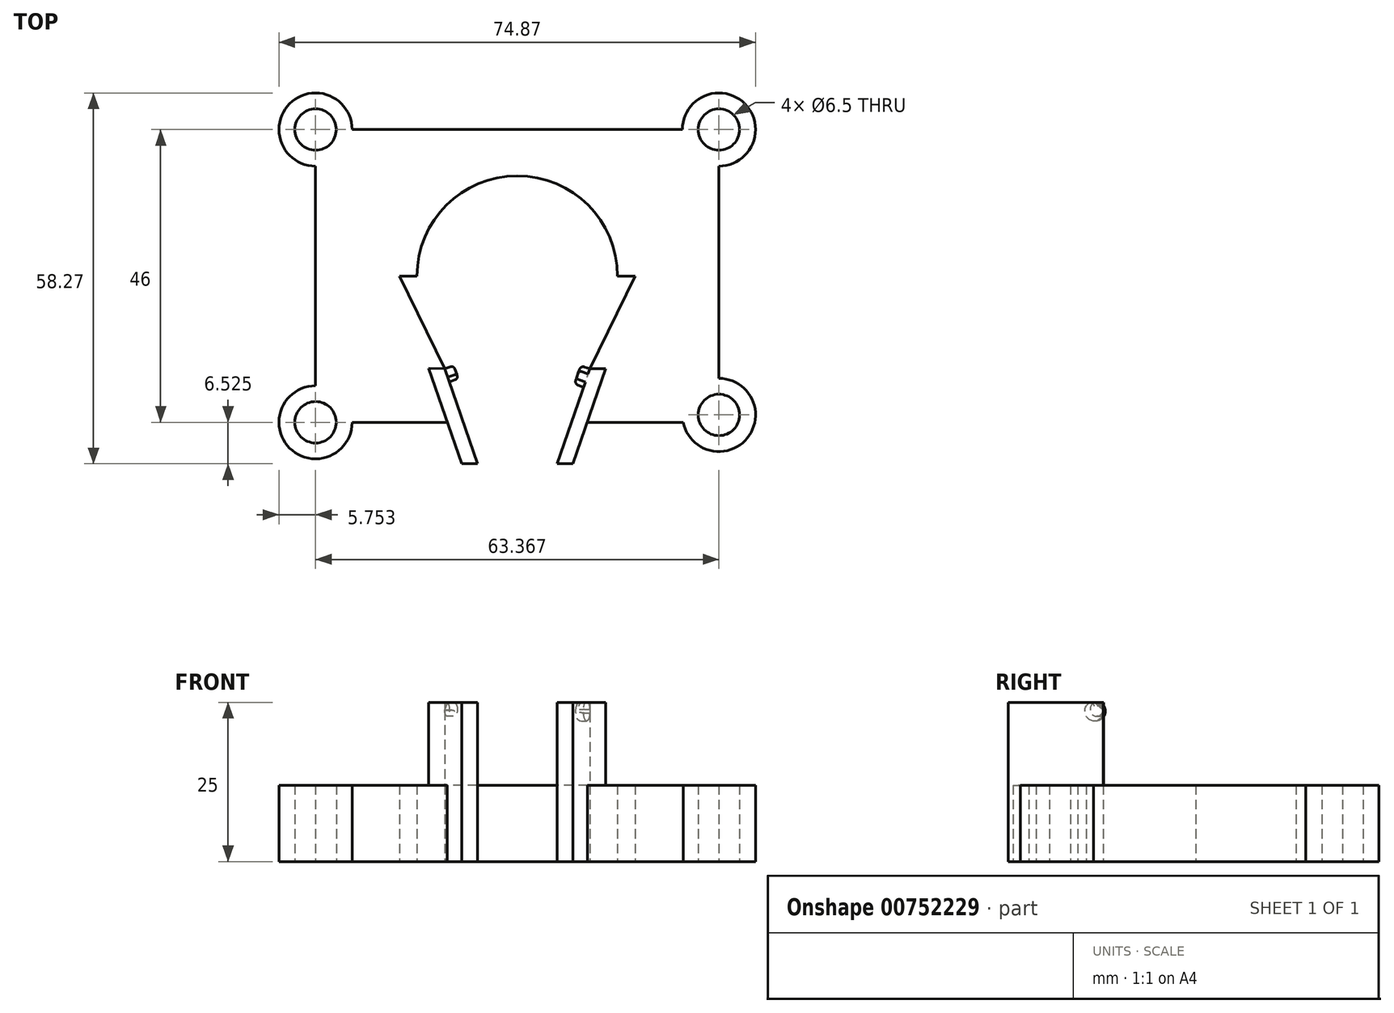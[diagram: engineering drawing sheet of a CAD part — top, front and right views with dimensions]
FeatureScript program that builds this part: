
annotation { "Feature Type Name" : "Feature", "Feature Type Description" : "" }
export const myFeature = defineFeature(function(context is Context, id is Id, definition is map)
    precondition{}
    {
        {
            var Q0;
            Q0=qCreatedBy(makeId("Top.planeOp"),FACE);
            var sketch = newSketch(context, id + "F0", { "sketchPlane" : qUnion([Q0])});
            skLineSegment(sketch, "E0.bottom", {"start": v(-52.57, 38.18) * mm, "end": v(4.3, 38.18) * mm});
            skLineSegment(sketch, "E0.left", {"start": v(-55.82, 34.93) * mm, "end": v(-55.82, -4.57) * mm});
            skLineSegment(sketch, "E0.right", {"start": v(7.55, 34.93) * mm, "end": v(7.55, -3.4) * mm});
            skCircle(sketch, "E1", {"center": v(7.55, 38.18) * mm, "radius": 3.25 * mm});
            skCircle(sketch, "E2", {"center": v(-55.82, 38.18) * mm, "radius": 3.25 * mm});
            skCircle(sketch, "E3", {"center": v(-55.82, -7.82) * mm, "radius": 3.25 * mm});
            skCircle(sketch, "E4", {"center": v(7.55, -6.66) * mm, "radius": 3.25 * mm});
            skCircle(sketch, "E5", {"center": v(-55.82, 38.18) * mm, "radius": 5.75 * mm});
            skCircle(sketch, "E6", {"center": v(7.55, 38.18) * mm, "radius": 5.75 * mm});
            skCircle(sketch, "E7", {"center": v(7.55, -6.66) * mm, "radius": 5.75 * mm});
            skCircle(sketch, "E8", {"center": v(-55.82, -7.82) * mm, "radius": 5.75 * mm});
            skPoint(sketch, "E9.first.point", {"position": v(-24.13, 38.18) * mm});
            skPoint(sketch, "E9.second.point", {"position": v(-55.82, 15.18) * mm});
            skPoint(sketch, "E10.middle", {"position": v(-24.13, 15.17) * mm});
            skCircle(sketch, "E11", {"center": v(-24.13, 15.17) * mm, "radius": 15.75 * mm});
            skArc(sketch, "E12", {"start": v(-5.63, 15.17) * mm, "mid": v(-24.13, 33.67) * mm, "end": v(-42.63, 15.17) * mm});
            skLineSegment(sketch, "E13", {"start": v(-24.13, -7.82) * mm, "end": v(-24.13, -7.85) * mm});
            skLineSegment(sketch, "E14", {"start": v(-35.53, 0.6) * mm, "end": v(-30.38, -14.34) * mm});
            skLineSegment(sketch, "E15", {"start": v(-17.88, -14.34) * mm, "end": v(-12.74, 0.6) * mm});
            skLineSegment(sketch, "E16", {"start": v(-30.38, -14.34) * mm, "end": v(-32.88, -14.34) * mm});
            skLineSegment(sketch, "E17", {"start": v(-32.88, -14.34) * mm, "end": v(-38.03, 0.64) * mm});
            skLineSegment(sketch, "E18", {"start": v(-38.03, 0.64) * mm, "end": v(-35.53, 0.6) * mm});
            skLineSegment(sketch, "E19", {"start": v(-17.88, -14.34) * mm, "end": v(-15.38, -14.34) * mm});
            skLineSegment(sketch, "E20", {"start": v(-15.38, -14.34) * mm, "end": v(-10.24, 0.6) * mm});
            skLineSegment(sketch, "E21", {"start": v(-10.24, 0.6) * mm, "end": v(-12.74, 0.6) * mm});
            skLineSegment(sketch, "E22.trimOffspring", {"start": v(-55.82, -7.82) * mm, "end": v(-55.82, -7.85) * mm});
            skLineSegment(sketch, "E23.trimOffspring", {"start": v(7.55, 38.18) * mm, "end": v(7.55, 38.18) * mm});
            skPoint(sketch, "E24.orphan", {"position": v(-24.13, -14.34) * mm});
            skLineSegment(sketch, "E25", {"start": v(-24.13, 15.17) * mm, "end": v(-42.63, 15.17) * mm});
            skLineSegment(sketch, "E26", {"start": v(-35.53, 0.6) * mm, "end": v(-42.63, 15.17) * mm});
            skLineSegment(sketch, "E27", {"start": v(-24.13, 15.17) * mm, "end": v(-5.63, 15.17) * mm});
            skLineSegment(sketch, "E28", {"start": v(-12.74, 0.6) * mm, "end": v(-5.63, 15.17) * mm});
            skLineSegment(sketch, "E29", {"start": v(-30.38, -14.34) * mm, "end": v(-17.88, -14.34) * mm});
            skLineSegment(sketch, "E30", {"start": v(-42.63, 15.17) * mm, "end": v(-55.82, 15.18) * mm});
            skLineSegment(sketch, "E31", {"start": v(-5.63, 15.17) * mm, "end": v(7.55, 15.17) * mm});
            skLineSegment(sketch, "E32", {"start": v(-24.13, 15.17) * mm, "end": v(-24.13, -14.34) * mm});
            skLineSegment(sketch, "E33", {"start": v(-24.13, 15.17) * mm, "end": v(-24.13, 38.18) * mm});
            skLineSegment(sketch, "E34", {"start": v(-35.53, 0.6) * mm, "end": v(-12.74, 0.6) * mm});
            skLineSegment(sketch, "E35", {"start": v(-24.13, -7.82) * mm, "end": v(1.92, -7.82) * mm});
            skLineSegment(sketch, "E36", {"start": v(-24.13, -7.82) * mm, "end": v(-50.07, -7.82) * mm});
            skSolve(sketch);
        }
        {
            var Q0;
            {var subQ0=sQuery(id+"F0.wireOp",EDGE,"E30");Q0=makeQuery(id+"F0.imprint","IMPRINT",FACE,{"disambiguationData":[TD([[makeQuery(id+"F0.imprint","IMPRINT",EDGE,{"derivedFrom":subQ0}),-1.0]])]});}
            var Q1;
            {var subQ0=sQuery(id+"F0.wireOp",EDGE,"E0.bottom");var subQ1=sQuery(id+"F0.wireOp",EDGE,"E2");var subQ2=makeQuery(id+"F0.imprint","INTERSECT",VERTEX,{"derivedFrom":[subQ1,subQ0]});Q1=makeQuery(id+"F0.imprint","IMPRINT",FACE,{"disambiguationData":[TD([[makeQuery(id+"F0.imprint","IMPRINT",EDGE,{"disambiguationData":[TD([[subQ2,1.0]])],"derivedFrom":subQ1}),-1.0]])]});}
            var Q2;
            {var subQ0=sQuery(id+"F0.wireOp",EDGE,"E0.bottom");var subQ1=sQuery(id+"F0.wireOp",EDGE,"E2");var subQ2=makeQuery(id+"F0.imprint","INTERSECT",VERTEX,{"derivedFrom":[subQ1,subQ0]});Q2=makeQuery(id+"F0.imprint","IMPRINT",FACE,{"disambiguationData":[TD([[makeQuery(id+"F0.imprint","IMPRINT",EDGE,{"disambiguationData":[TD([[subQ2,-1.0]])],"derivedFrom":subQ1}),-1.0]])]});}
            var Q3;
            {var subQ0=sQuery(id+"F0.wireOp",EDGE,"E31");Q3=makeQuery(id+"F0.imprint","IMPRINT",FACE,{"disambiguationData":[TD([[makeQuery(id+"F0.imprint","IMPRINT",EDGE,{"derivedFrom":subQ0}),1.0]])]});}
            var Q4;
            {var subQ0=sQuery(id+"F0.wireOp",EDGE,"E33");var subQ1=sQuery(id+"F0.wireOp",EDGE,"E11");var subQ2=makeQuery(id+"F0.imprint","INTERSECT",VERTEX,{"derivedFrom":[subQ1,subQ0]});Q4=makeQuery(id+"F0.imprint","IMPRINT",FACE,{"disambiguationData":[TD([[makeQuery(id+"F0.imprint","IMPRINT",EDGE,{"disambiguationData":[TD([[subQ2,1.0]])],"derivedFrom":subQ1}),-1.0]])]});}
            var Q5;
            {var subQ0=sQuery(id+"F0.wireOp",EDGE,"E33");var subQ1=sQuery(id+"F0.wireOp",EDGE,"E11");var subQ2=makeQuery(id+"F0.imprint","INTERSECT",VERTEX,{"derivedFrom":[subQ1,subQ0]});Q5=makeQuery(id+"F0.imprint","IMPRINT",FACE,{"disambiguationData":[TD([[makeQuery(id+"F0.imprint","IMPRINT",EDGE,{"disambiguationData":[TD([[subQ2,-1.0]])],"derivedFrom":subQ1}),-1.0]])]});}
            var Q6;
            {var subQ0=sQuery(id+"F0.wireOp",EDGE,"E0.bottom");var subQ1=sQuery(id+"F0.wireOp",EDGE,"E1");var subQ2=makeQuery(id+"F0.imprint","INTERSECT",VERTEX,{"derivedFrom":[subQ1,subQ0]});Q6=makeQuery(id+"F0.imprint","IMPRINT",FACE,{"disambiguationData":[TD([[makeQuery(id+"F0.imprint","IMPRINT",EDGE,{"disambiguationData":[TD([[subQ2,1.0]])],"derivedFrom":subQ1}),-1.0]])]});}
            var Q7;
            {var subQ0=sQuery(id+"F0.wireOp",EDGE,"E0.bottom");var subQ1=sQuery(id+"F0.wireOp",EDGE,"E1");var subQ2=makeQuery(id+"F0.imprint","INTERSECT",VERTEX,{"derivedFrom":[subQ1,subQ0]});Q7=makeQuery(id+"F0.imprint","IMPRINT",FACE,{"disambiguationData":[TD([[makeQuery(id+"F0.imprint","IMPRINT",EDGE,{"disambiguationData":[TD([[subQ2,-1.0]])],"derivedFrom":subQ1}),-1.0]])]});}
            var Q8;
            {var subQ0=sQuery(id+"F0.wireOp",EDGE,"E0.right");var subQ1=sQuery(id+"F0.wireOp",EDGE,"E4");var subQ2=makeQuery(id+"F0.imprint","INTERSECT",VERTEX,{"derivedFrom":[subQ1,subQ0]});Q8=makeQuery(id+"F0.imprint","IMPRINT",FACE,{"disambiguationData":[TD([[makeQuery(id+"F0.imprint","IMPRINT",EDGE,{"disambiguationData":[TD([[subQ2,1.0]])],"derivedFrom":subQ1}),-1.0]])]});}
            var Q9;
            {var subQ0=sQuery(id+"F0.wireOp",EDGE,"E0.right");var subQ1=sQuery(id+"F0.wireOp",EDGE,"E4");var subQ2=makeQuery(id+"F0.imprint","INTERSECT",VERTEX,{"derivedFrom":[subQ1,subQ0]});Q9=makeQuery(id+"F0.imprint","IMPRINT",FACE,{"disambiguationData":[TD([[makeQuery(id+"F0.imprint","IMPRINT",EDGE,{"disambiguationData":[TD([[subQ2,-1.0]])],"derivedFrom":subQ1}),-1.0]])]});}
            var Q10;
            Q10=makeQuery(id+"F0.imprint","IMPRINT",FACE,{"disambiguationData":[TD([[makeQuery(id+"F0.imprint","IMPRINT",EDGE,{"derivedFrom":sQuery(id+"F0.wireOp",EDGE,"E15")}),-1.0]])]});
            var Q11;
            {var subQ0=sQuery(id+"F0.wireOp",EDGE,"E21");Q11=makeQuery(id+"F0.imprint","IMPRINT",FACE,{"disambiguationData":[TD([[makeQuery(id+"F0.imprint","IMPRINT",EDGE,{"derivedFrom":subQ0}),-1.0]])]});}
            var Q12;
            {var subQ8=sQuery(id+"F0.wireOp",EDGE,"E18");Q12=makeQuery(id+"F0.imprint","IMPRINT",FACE,{"disambiguationData":[TD([[makeQuery(id+"F0.imprint","IMPRINT",EDGE,{"derivedFrom":subQ8}),1.0]])]});}
            var Q13;
            {var subQ0=sQuery(id+"F0.wireOp",EDGE,"E3");var subQ1=sQuery(id+"F0.wireOp",EDGE,"E0.top");var subQ2=makeQuery(id+"F0.imprint","INTERSECT",VERTEX,{"derivedFrom":[subQ1,subQ0]});Q13=makeQuery(id+"F0.imprint","IMPRINT",FACE,{"disambiguationData":[TD([[makeQuery(id+"F0.imprint","IMPRINT",EDGE,{"disambiguationData":[TD([[subQ2,-1.0]])],"derivedFrom":subQ1}),1.0]])]});}
            var Q14;
            {var subQ0=sQuery(id+"F0.wireOp",EDGE,"E10.top");var subQ1=sQuery(id+"F0.wireOp",EDGE,"E3");var subQ2=makeQuery(id+"F0.imprint","INTERSECT",VERTEX,{"derivedFrom":[subQ1,subQ0]});Q14=makeQuery(id+"F0.imprint","IMPRINT",FACE,{"disambiguationData":[TD([[makeQuery(id+"F0.imprint","IMPRINT",EDGE,{"disambiguationData":[TD([[subQ2,1.0]])],"derivedFrom":subQ1}),-1.0]])]});}
            var Q15;
            Q15=makeQuery(id+"F0.imprint","IMPRINT",FACE,{"disambiguationData":[TD([[makeQuery(id+"F0.imprint","IMPRINT",EDGE,{"derivedFrom":sQuery(id+"F0.wireOp",EDGE,"E14")}),-1.0]])]});
            extrude(context, id + "F1", {"entities" : qUnion([Q0, Q1, Q2, Q3, Q4, Q5, Q6, Q7, Q8, Q9, Q10, Q11, Q12, Q13, Q14, Q15]), "depth" : 12 * mm, "offsetDistance" : 25 * mm});
        }
        {
            var Q0;
            Q0=makeQuery(id+"F0.imprint","IMPRINT",FACE,{"disambiguationData":[TD([[makeQuery(id+"F0.imprint","IMPRINT",EDGE,{"derivedFrom":sQuery(id+"F0.wireOp",EDGE,"E14")}),-1.0]])]});
            var Q1;
            Q1=makeQuery(id+"F0.imprint","IMPRINT",FACE,{"disambiguationData":[TD([[makeQuery(id+"F0.imprint","IMPRINT",EDGE,{"derivedFrom":sQuery(id+"F0.wireOp",EDGE,"E15")}),-1.0]])]});
            extrude(context, id + "F2", {"entities" : qUnion([Q0, Q1]), "operationType" : NewBodyOperationType.ADD, "depth" : 25 * mm, "offsetDistance" : 25 * mm});
        }
        {
            var Q0;
            {var subQ0=sQuery(id+"F0.wireOp",EDGE,"E14");Q0=makeQuery(id+"F2.boolean.opBoolean","MERGE",FACE,{"derivedFrom":[makeQuery(id+"F1.opExtrude","SWEPT_FACE",FACE,{"disambiguationData":[OSD([subQ0])]}),makeQuery(id+"F2.opExtrude","SWEPT_FACE",FACE,{"disambiguationData":[OSD([subQ0])]})]});}
            var sketch = newSketch(context, id + "F3", { "sketchPlane" : qUnion([Q0])});
            skSolve(sketch);
        }
        {
            var Q0;
            {var subQ2=sQuery(id+"F0.wireOp",EDGE,"E14");Q0=makeQuery(id+"F3.imprint","IMPRINT",FACE,{"disambiguationData":[TD([[makeQuery(id+"F3.imprint","IMPRINT",EDGE,{"derivedFrom":makeQuery(id+"F1.opExtrude","CAP_EDGE",EDGE,{"disambiguationData":[OSD([subQ2])],"isStart":true})}),-1.0]])]});}
            var sketch = newSketch(context, id + "F4", { "sketchPlane" : qUnion([Q0])});
            skArc(sketch, "E37", {"start": v(10.74, 24.97) * mm, "mid": v(10.35, 23.1) * mm, "end": v(12.14, 23.77) * mm});
            skLineSegment(sketch, "E38", {"start": v(12.14, 23.77) * mm, "end": v(10.74, 24.97) * mm});
            skSolve(sketch);
        }
        {
            var Q0;
            {var subQ0=sQuery(id+"F4.wireOp",EDGE,"E38");var subQ1=sQuery(id+"F4.wireOp",EDGE,"E37");var subQ2=makeQuery(id+"F4.imprint","INTERSECT",VERTEX,{"disambiguationData":[OD(0.0)],"derivedFrom":[subQ1,subQ0]});Q0=makeQuery(id+"F4.imprint","IMPRINT",FACE,{"disambiguationData":[TD([[makeQuery(id+"F4.imprint","IMPRINT",EDGE,{"disambiguationData":[TD([[subQ2,-1.0]])],"derivedFrom":subQ1}),1.0]])]});}
            extrude(context, id + "F5", {"entities" : qUnion([Q0]), "operationType" : NewBodyOperationType.ADD, "depth" : 1.5 * mm, "offsetDistance" : 25 * mm});
        }
        {
            var Q0;
            Q0=makeQuery(id+"F5.opExtrude","CAP_EDGE",EDGE,{"disambiguationData":[OSD([sQuery(id+"F4.wireOp",EDGE,"E38")])],"isStart":false});
            var Q1;
            Q1=makeQuery(id+"F5.opExtrude","CAP_EDGE",EDGE,{"disambiguationData":[OSD([sQuery(id+"F4.wireOp",EDGE,"E37")])],"isStart":false});
            fillet(context, id + "F6", {"entities" : qUnion([Q0, Q1]), "radius" : 0.5 * mm, "tangentPropagation" : true, "allowEdgeOverflow" : false});
        }
        {
            var Q0;
            {var subQ0=sQuery(id+"F0.wireOp",EDGE,"E15");Q0=makeQuery(id+"F2.boolean.opBoolean","MERGE",FACE,{"derivedFrom":[makeQuery(id+"F1.opExtrude","SWEPT_FACE",FACE,{"disambiguationData":[OSD([subQ0])]}),makeQuery(id+"F2.opExtrude","SWEPT_FACE",FACE,{"disambiguationData":[OSD([subQ0])]})]});}
            var sketch = newSketch(context, id + "F7", { "sketchPlane" : qUnion([Q0])});
            skCircle(sketch, "E39", {"center": v(5.1, 23.62) * mm, "radius": 1.53 * mm});
            skPoint(sketch, "E39.first.point", {"position": v(5.77, 25) * mm});
            skPoint(sketch, "E39.second.point", {"position": v(3.6, 23.36) * mm});
            skPoint(sketch, "E39.third.point", {"position": v(6.31, 22.69) * mm});
            skSolve(sketch);
        }
        {
            var Q0;
            {var subQ0=sQuery(id+"F7.wireOp",EDGE,"E39");var subQ1=sQuery(id+"F0.wireOp",EDGE,"E15");var subQ2=makeQuery(id+"F2.opExtrude","CAP_EDGE",EDGE,{"disambiguationData":[OSD([subQ1])],"isStart":false});var subQ3=makeQuery(id+"F7.imprint","INTERSECT",VERTEX,{"disambiguationData":[OD(0.0)],"derivedFrom":[subQ2,subQ0]});Q0=makeQuery(id+"F7.imprint","IMPRINT",FACE,{"disambiguationData":[TD([[makeQuery(id+"F7.imprint","IMPRINT",EDGE,{"disambiguationData":[TD([[subQ3,1.0]])],"derivedFrom":subQ2}),1.0]])]});}
            extrude(context, id + "F8", {"entities" : qUnion([Q0]), "operationType" : NewBodyOperationType.ADD, "depth" : 1.5 * mm, "offsetDistance" : 25 * mm});
        }
        {
            var Q0;
            Q0=makeQuery(id+"F8.opExtrude","CAP_EDGE",EDGE,{"disambiguationData":[OSD([sQuery(id+"F0.wireOp",EDGE,"E15")])],"isStart":false});
            var Q1;
            Q1=makeQuery(id+"F8.opExtrude","CAP_FACE",FACE,{"disambiguationData":[OSD([sQuery(id+"F0.wireOp",EDGE,"E15"),sQuery(id+"F0.wireOp",EDGE,"E21"),sQuery(id+"F0.wireOp",EDGE,"E28"),sQuery(id+"F0.wireOp",EDGE,"E34"),sQuery(id+"F7.wireOp",EDGE,"E39")])],"isStart":false});
            var Q2;
            {var subQ0=sQuery(id+"F7.wireOp",EDGE,"E39");var subQ1=sQuery(id+"F0.wireOp",EDGE,"E15");Q2=makeQuery(id+"F8.opExtrude","CAP_EDGE",EDGE,{"disambiguationData":[OSD([subQ0]),TDD([makeQuery(id+"F7.imprint","IMPRINT",EDGE,{"disambiguationData":[TD([[makeQuery(id+"F7.imprint","INTERSECT",VERTEX,{"disambiguationData":[OD(1.0)],"derivedFrom":[makeQuery(id+"F2.opExtrude","CAP_EDGE",EDGE,{"disambiguationData":[OSD([subQ1])],"isStart":false}),subQ0]}),1.0]])],"derivedFrom":subQ0})])],"isStart":false});}
            fillet(context, id + "F9", {"entities" : qUnion([Q0, Q1, Q2]), "radius" : 0.6 * mm, "tangentPropagation" : true, "allowEdgeOverflow" : false});
        }
    });
